# Revit family: ZUMBADOR
name_source: partatom
category: Electrical Fixtures
units: mm (PartAtom-declared; Revit-internal decimal feet)

## family parameters
Always vertical = No
Cut with Voids When Loaded = No
Maintain Annotation Orientation = Yes
Part Type = Normal
Room Calculation Point = No
Round Connector Dimension = Use Diameter
Shared = Yes
Work Plane-Based = Yes

## types (1)
- ZUMBADOR
    ANCHO = 36 mm
    ANCHO BASE = 37 mm
    ANCHO CONECTOR = 26 mm  [stored 0.0853018 ft]
    ANCHO RANURA = 2 mm  [stored 0.00656168 ft]
    ANCHO ZUMBADOR = 18 mm  [stored 0.0590551 ft]
    Default Elevation = 1219 mm
    ESPESOR = 8 mm  [stored 0.0262467 ft]
    ESPESOR BASE = 3 mm  [stored 0.00984252 ft]
    ESPESOR CONECTOR = 10 mm  [stored 0.0328084 ft]
    INCLUIR EN LISTADO = No
    LARGO BASE = 66 mm  [stored 0.216535 ft]
    LARGO CONECTOR = 50 mm  [stored 0.164042 ft]
    LARGO ZUMBADOR = 41 mm  [stored 0.134514 ft]
    LONGITUD = 65 mm  [stored 0.213255 ft]
    OFFSET = 0 mm  [stored 0 ft]
    PROFUNDIDAD RANURA = 2 mm  [stored 0.00656168 ft]
    RADIO_1 = 1 mm  [stored 0.00328084 ft]
    RADIO_2 = 1 mm  [stored 0.00328084 ft]
    RADIO_3 = 2 mm  [stored 0.00656168 ft]
    SEP BORDE = 2 mm  [stored 0.00656168 ft]
    SEP RANURAS = 2 mm  [stored 0.00656168 ft]

note: [stored X ft] marks values corroborated as IEEE doubles in the binary element streams (Revit-internal decimal feet)

## geometry (parser evidence)
native form markers: Sweep x9
no freeform markers — native parametric forms only
